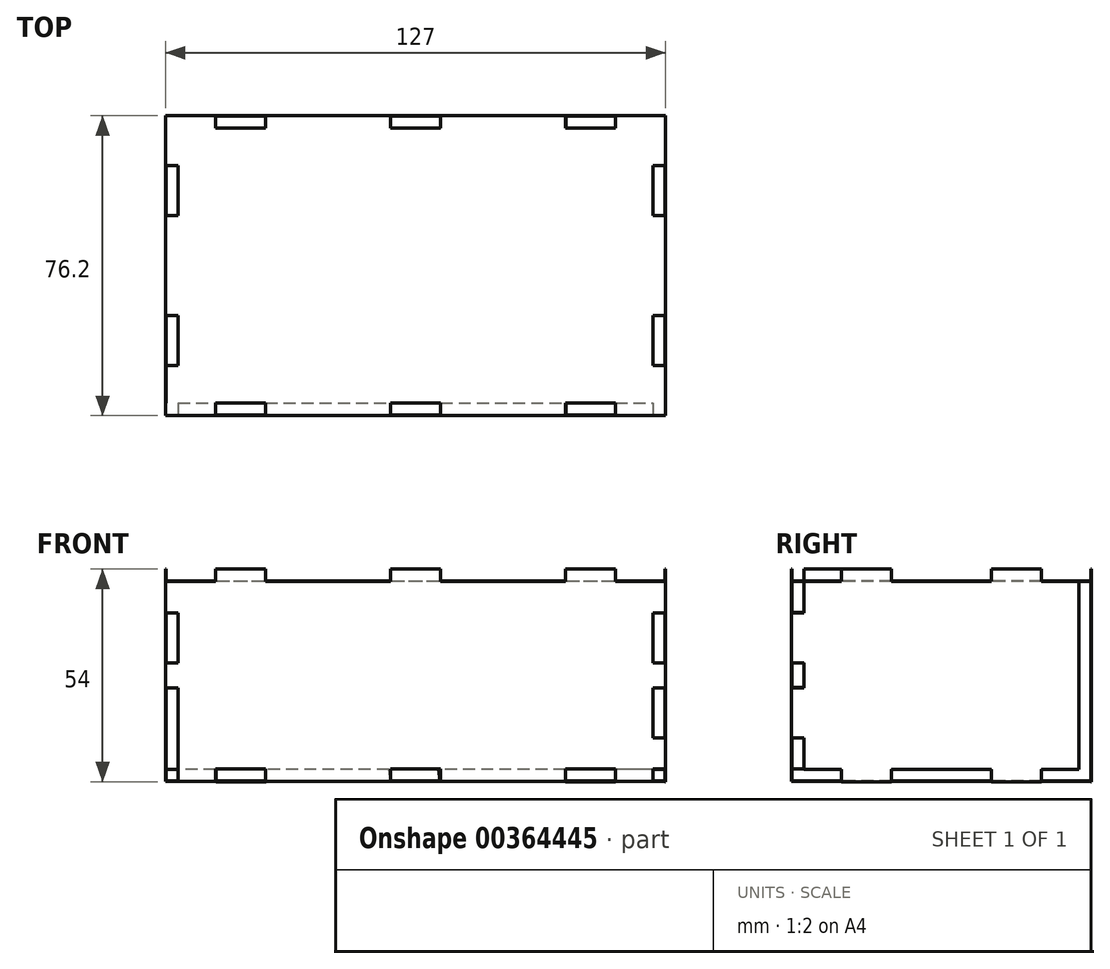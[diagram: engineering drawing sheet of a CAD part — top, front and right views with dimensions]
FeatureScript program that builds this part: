
annotation { "Feature Type Name" : "Feature", "Feature Type Description" : "" }
export const myFeature = defineFeature(function(context is Context, id is Id, definition is map)
    precondition{}
    {
        {
            assignVariable(context, id + "F0", {"name" : "ply", "anyValue" : .125});
        }
        {
            var Q0;
            Q0=qCreatedBy(makeId("Top.planeOp"),FACE);
            var sketch = newSketch(context, id + "F1", { "sketchPlane" : qUnion([Q0])});
            skLineSegment(sketch, "E0.bottom", {"start": v(-63.5, 38.1) * mm, "end": v(63.5, 38.1) * mm});
            skLineSegment(sketch, "E0.top", {"start": v(-63.5, -38.1) * mm, "end": v(63.5, -38.1) * mm});
            skLineSegment(sketch, "E0.left", {"start": v(-63.5, 38.1) * mm, "end": v(-63.5, -38.1) * mm});
            skLineSegment(sketch, "E0.right", {"start": v(63.5, 38.1) * mm, "end": v(63.5, -38.1) * mm});
            skPoint(sketch, "E0.middle", {"position": v(0, 0) * mm});
            skSolve(sketch);
        }
        {
            var Q0;
            Q0=makeQuery(id+"F1.imprint","IMPRINT",FACE,{"disambiguationData":[TD([[makeQuery(id+"F1.imprint","IMPRINT",EDGE,{"derivedFrom":sQuery(id+"F1.wireOp",EDGE,"E0.bottom")}),-1.0]])]});
            extrude(context, id + "F2", {"entities" : qUnion([Q0]), "depth" : (getVariable(context, 'ply')) * mm});
        }
        {
            var Q0;
            Q0=makeQuery(id+"F2.opExtrude","CAP_FACE",FACE,{"disambiguationData":[OSD([sQuery(id+"F1.wireOp",EDGE,"E0.bottom"),sQuery(id+"F1.wireOp",EDGE,"E0.top"),sQuery(id+"F1.wireOp",EDGE,"E0.left"),sQuery(id+"F1.wireOp",EDGE,"E0.right")])],"isStart":false});
            var sketch = newSketch(context, id + "F3", { "sketchPlane" : qUnion([Q0])});
            skLineSegment(sketch, "E1.bottom", {"start": v(-63.5, -25.4) * mm, "end": v(-60.33, -25.4) * mm});
            skLineSegment(sketch, "E1.top", {"start": v(-63.5, -12.7) * mm, "end": v(-60.33, -12.7) * mm});
            skLineSegment(sketch, "E1.left", {"start": v(-63.5, -25.4) * mm, "end": v(-63.5, -12.7) * mm});
            skLineSegment(sketch, "E1.right", {"start": v(-60.33, -25.4) * mm, "end": v(-60.33, -12.7) * mm});
            skLineSegment(sketch, "E2.bottom", {"start": v(-63.5, 12.7) * mm, "end": v(-60.33, 12.7) * mm});
            skLineSegment(sketch, "E2.top", {"start": v(-63.5, 25.4) * mm, "end": v(-60.33, 25.4) * mm});
            skLineSegment(sketch, "E2.left", {"start": v(-63.5, 12.7) * mm, "end": v(-63.5, 25.4) * mm});
            skLineSegment(sketch, "E2.right", {"start": v(-60.33, 12.7) * mm, "end": v(-60.33, 25.4) * mm});
            skSolve(sketch);
        }
        {
            var Q0;
            Q0=makeQuery(id+"F3.imprint","IMPRINT",FACE,{"disambiguationData":[TD([[makeQuery(id+"F3.imprint","IMPRINT",EDGE,{"derivedFrom":sQuery(id+"F3.wireOp",EDGE,"E1.bottom")}),1.0]])]});
            var Q1;
            Q1=makeQuery(id+"F3.imprint","IMPRINT",FACE,{"disambiguationData":[TD([[makeQuery(id+"F3.imprint","IMPRINT",EDGE,{"derivedFrom":sQuery(id+"F3.wireOp",EDGE,"E2.bottom")}),1.0]])]});
            extrude(context, id + "F4", {"entities" : qUnion([Q0, Q1]), "operationType" : NewBodyOperationType.REMOVE, "endBound" : BoundingType.UP_TO_NEXT, "oppositeDirection" : true, "depth" : 25.4 * mm});
        }
        {
            var Q0;
            Q0=makeQuery(id+"F2.opExtrude","CAP_FACE",FACE,{"disambiguationData":[OSD([sQuery(id+"F1.wireOp",EDGE,"E0.bottom"),sQuery(id+"F1.wireOp",EDGE,"E0.top"),sQuery(id+"F1.wireOp",EDGE,"E0.left"),sQuery(id+"F1.wireOp",EDGE,"E0.right")])],"isStart":false});
            var sketch = newSketch(context, id + "F5", { "sketchPlane" : qUnion([Q0])});
            skLineSegment(sketch, "E3.bottom", {"start": v(63.5, 25.4) * mm, "end": v(60.33, 25.4) * mm});
            skLineSegment(sketch, "E3.top", {"start": v(63.5, 12.7) * mm, "end": v(60.33, 12.7) * mm});
            skLineSegment(sketch, "E3.left", {"start": v(63.5, 25.4) * mm, "end": v(63.5, 12.7) * mm});
            skLineSegment(sketch, "E3.right", {"start": v(60.33, 25.4) * mm, "end": v(60.33, 12.7) * mm});
            skLineSegment(sketch, "E4.bottom", {"start": v(63.5, -12.7) * mm, "end": v(60.33, -12.7) * mm});
            skLineSegment(sketch, "E4.top", {"start": v(63.5, -25.4) * mm, "end": v(60.33, -25.4) * mm});
            skLineSegment(sketch, "E4.left", {"start": v(63.5, -12.7) * mm, "end": v(63.5, -25.4) * mm});
            skLineSegment(sketch, "E4.right", {"start": v(60.33, -12.7) * mm, "end": v(60.33, -25.4) * mm});
            skSolve(sketch);
        }
        {
            var Q0;
            Q0=makeQuery(id+"F5.imprint","IMPRINT",FACE,{"disambiguationData":[TD([[makeQuery(id+"F5.imprint","IMPRINT",EDGE,{"derivedFrom":sQuery(id+"F5.wireOp",EDGE,"E3.bottom")}),1.0]])]});
            var Q1;
            Q1=makeQuery(id+"F5.imprint","IMPRINT",FACE,{"disambiguationData":[TD([[makeQuery(id+"F5.imprint","IMPRINT",EDGE,{"derivedFrom":sQuery(id+"F5.wireOp",EDGE,"E4.bottom")}),1.0]])]});
            extrude(context, id + "F6", {"entities" : qUnion([Q0, Q1]), "operationType" : NewBodyOperationType.REMOVE, "endBound" : BoundingType.UP_TO_NEXT, "oppositeDirection" : true, "depth" : 25.4 * mm});
        }
        {
            var Q0;
            Q0=makeQuery(id+"F2.opExtrude","CAP_FACE",FACE,{"disambiguationData":[OSD([sQuery(id+"F1.wireOp",EDGE,"E0.bottom"),sQuery(id+"F1.wireOp",EDGE,"E0.top"),sQuery(id+"F1.wireOp",EDGE,"E0.left"),sQuery(id+"F1.wireOp",EDGE,"E0.right")])],"isStart":false});
            var sketch = newSketch(context, id + "F7", { "sketchPlane" : qUnion([Q0])});
            skLineSegment(sketch, "E5.bottom", {"start": v(-50.8, 38.1) * mm, "end": v(-38.1, 38.1) * mm});
            skLineSegment(sketch, "E5.top", {"start": v(-50.8, 34.93) * mm, "end": v(-38.1, 34.93) * mm});
            skLineSegment(sketch, "E5.left", {"start": v(-50.8, 38.1) * mm, "end": v(-50.8, 34.93) * mm});
            skLineSegment(sketch, "E5.right", {"start": v(-38.1, 38.1) * mm, "end": v(-38.1, 34.93) * mm});
            skLineSegment(sketch, "E6.bottom", {"start": v(-6.35, 38.1) * mm, "end": v(6.35, 38.1) * mm});
            skLineSegment(sketch, "E6.top", {"start": v(-6.35, 34.93) * mm, "end": v(6.35, 34.93) * mm});
            skLineSegment(sketch, "E6.left", {"start": v(-6.35, 38.1) * mm, "end": v(-6.35, 34.93) * mm});
            skLineSegment(sketch, "E6.right", {"start": v(6.35, 38.1) * mm, "end": v(6.35, 34.93) * mm});
            skLineSegment(sketch, "E7.bottom", {"start": v(38.1, 38.1) * mm, "end": v(50.8, 38.1) * mm});
            skLineSegment(sketch, "E7.top", {"start": v(38.1, 34.93) * mm, "end": v(50.8, 34.93) * mm});
            skLineSegment(sketch, "E7.left", {"start": v(38.1, 38.1) * mm, "end": v(38.1, 34.93) * mm});
            skLineSegment(sketch, "E7.right", {"start": v(50.8, 38.1) * mm, "end": v(50.8, 34.93) * mm});
            skSolve(sketch);
        }
        {
            var Q0;
            Q0=makeQuery(id+"F7.imprint","IMPRINT",FACE,{"disambiguationData":[TD([[makeQuery(id+"F7.imprint","IMPRINT",EDGE,{"derivedFrom":sQuery(id+"F7.wireOp",EDGE,"E5.top")}),-1.0]])]});
            var sketch = newSketch(context, id + "F8", { "sketchPlane" : qUnion([Q0])});
            skLineSegment(sketch, "E8.bottom", {"start": v(-50.8, -38.1) * mm, "end": v(-38.1, -38.1) * mm});
            skLineSegment(sketch, "E8.top", {"start": v(-50.8, -34.93) * mm, "end": v(-38.1, -34.93) * mm});
            skLineSegment(sketch, "E8.left", {"start": v(-50.8, -38.1) * mm, "end": v(-50.8, -34.93) * mm});
            skLineSegment(sketch, "E8.right", {"start": v(-38.1, -38.1) * mm, "end": v(-38.1, -34.93) * mm});
            skPoint(sketch, "E9.firstSnap0", {"position": v(-44.45, -38.1) * mm});
            skLineSegment(sketch, "E9.bottom", {"start": v(-6.35, -38.1) * mm, "end": v(6.35, -38.1) * mm});
            skLineSegment(sketch, "E9.top", {"start": v(-6.35, -34.93) * mm, "end": v(6.35, -34.93) * mm});
            skLineSegment(sketch, "E9.left", {"start": v(6.35, -38.1) * mm, "end": v(6.35, -34.93) * mm});
            skLineSegment(sketch, "E9.right", {"start": v(-6.35, -38.1) * mm, "end": v(-6.35, -34.93) * mm});
            skLineSegment(sketch, "E10.bottom", {"start": v(38.1, -38.1) * mm, "end": v(50.8, -38.1) * mm});
            skLineSegment(sketch, "E10.top", {"start": v(38.1, -34.93) * mm, "end": v(50.8, -34.93) * mm});
            skLineSegment(sketch, "E10.left", {"start": v(50.8, -38.1) * mm, "end": v(50.8, -34.93) * mm});
            skLineSegment(sketch, "E10.right", {"start": v(38.1, -38.1) * mm, "end": v(38.1, -34.93) * mm});
            skSolve(sketch);
        }
        {
            var Q0;
            Q0 = qSketchRegion(id + "F7", true);
            extrude(context, id + "F9", {"entities" : qUnion([Q0]), "operationType" : NewBodyOperationType.REMOVE, "endBound" : BoundingType.UP_TO_NEXT, "oppositeDirection" : true, "depth" : 25.4 * mm});
        }
        {
            var Q0;
            Q0 = qSketchRegion(id + "F8", true);
            extrude(context, id + "F10", {"entities" : qUnion([Q0]), "operationType" : NewBodyOperationType.REMOVE, "endBound" : BoundingType.UP_TO_NEXT, "oppositeDirection" : true, "depth" : 25.4 * mm});
        }
        {
            var Q0;
            {var subQ1=sQuery(id+"F1.wireOp",EDGE,"E0.left");var subQ2=sQuery(id+"F1.wireOp",EDGE,"E0.top");Q0=makeQuery(id+"F10.boolean.opBoolean","SPLIT",FACE,{"disambiguationData":[TD([makeQuery(id+"F2.opExtrude","SWEPT_FACE",FACE,{"disambiguationData":[OSD([subQ1])]})])],"derivedFrom":makeQuery(id+"F2.opExtrude","SWEPT_FACE",FACE,{"disambiguationData":[OSD([subQ2])]})});}
            var sketch = newSketch(context, id + "F11", { "sketchPlane" : qUnion([Q0])});
            skLineSegment(sketch, "E11.bottom", {"start": v(-50.8, 3.18) * mm, "end": v(-38.1, 3.18) * mm});
            skLineSegment(sketch, "E11.top", {"start": v(-63.5, -50.8) * mm, "end": v(63.5, -50.8) * mm});
            skLineSegment(sketch, "E11.left", {"start": v(-63.5, 0) * mm, "end": v(-63.5, -50.8) * mm});
            skLineSegment(sketch, "E11.right", {"start": v(63.5, 3.18) * mm, "end": v(63.5, -50.8) * mm});
            skLineSegment(sketch, "E12.top", {"start": v(-63.5, 0) * mm, "end": v(-50.8, 0) * mm});
            skLineSegment(sketch, "E12.right", {"start": v(-50.8, 3.18) * mm, "end": v(-50.8, 0) * mm});
            skLineSegment(sketch, "E13.top", {"start": v(-38.1, 0) * mm, "end": v(-6.35, 0) * mm});
            skLineSegment(sketch, "E13.left", {"start": v(-38.1, 3.18) * mm, "end": v(-38.1, 0) * mm});
            skLineSegment(sketch, "E13.right", {"start": v(-6.35, 3.18) * mm, "end": v(-6.35, 0) * mm});
            skLineSegment(sketch, "E14.top", {"start": v(6.35, 0) * mm, "end": v(38.1, 0) * mm});
            skLineSegment(sketch, "E14.left", {"start": v(6.35, 3.18) * mm, "end": v(6.35, 0) * mm});
            skLineSegment(sketch, "E14.right", {"start": v(38.1, 3.18) * mm, "end": v(38.1, 0) * mm});
            skLineSegment(sketch, "E15.top", {"start": v(50.8, 0) * mm, "end": v(63.5, 0) * mm});
            skLineSegment(sketch, "E15.left", {"start": v(50.8, 3.18) * mm, "end": v(50.8, 0) * mm});
            skLineSegment(sketch, "E15.right", {"start": v(63.5, 3.18) * mm, "end": v(63.5, 0) * mm});
            skPoint(sketch, "E12.left.start.orphan", {"position": v(-63.5, 3.18) * mm});
            skLineSegment(sketch, "E16.trimOffspring", {"start": v(-6.35, 3.18) * mm, "end": v(6.35, 3.18) * mm});
            skLineSegment(sketch, "E17.trimOffspring", {"start": v(38.1, 3.18) * mm, "end": v(50.8, 3.18) * mm});
            skSolve(sketch);
        }
        {
            var Q0;
            Q0=makeQuery(id+"F11.imprint","IMPRINT",FACE,{"disambiguationData":[TD([[makeQuery(id+"F11.imprint","IMPRINT",EDGE,{"derivedFrom":sQuery(id+"F11.wireOp",EDGE,"E11.bottom")}),-1.0]])]});
            extrude(context, id + "F12", {"entities" : qUnion([Q0]), "oppositeDirection" : true, "depth" : (getVariable(context, 'ply')) * mm});
        }
        {
            var Q0;
            Q0=makeQuery(id+"F12.opExtrude","CAP_FACE",FACE,{"disambiguationData":[OSD([sQuery(id+"F11.wireOp",EDGE,"E11.bottom"),sQuery(id+"F11.wireOp",EDGE,"E11.top"),sQuery(id+"F11.wireOp",EDGE,"E11.left"),sQuery(id+"F11.wireOp",EDGE,"E11.right"),sQuery(id+"F11.wireOp",EDGE,"E12.top"),sQuery(id+"F11.wireOp",EDGE,"E12.right"),sQuery(id+"F11.wireOp",EDGE,"E13.top"),sQuery(id+"F11.wireOp",EDGE,"E13.left"),sQuery(id+"F11.wireOp",EDGE,"E13.right"),sQuery(id+"F11.wireOp",EDGE,"E14.top"),sQuery(id+"F11.wireOp",EDGE,"E14.left"),sQuery(id+"F11.wireOp",EDGE,"E14.right"),sQuery(id+"F11.wireOp",EDGE,"E15.top"),sQuery(id+"F11.wireOp",EDGE,"E15.left"),sQuery(id+"F11.wireOp",EDGE,"E16.trimOffspring"),sQuery(id+"F11.wireOp",EDGE,"E17.trimOffspring")])],"isStart":true});
            var sketch = newSketch(context, id + "F13", { "sketchPlane" : qUnion([Q0])});
            skLineSegment(sketch, "E18.bottom", {"start": v(-50.8, -50.8) * mm, "end": v(-38.1, -50.8) * mm});
            skLineSegment(sketch, "E18.top", {"start": v(-50.8, -47.63) * mm, "end": v(-38.1, -47.63) * mm});
            skLineSegment(sketch, "E18.left", {"start": v(-50.8, -50.8) * mm, "end": v(-50.8, -47.63) * mm});
            skLineSegment(sketch, "E18.right", {"start": v(-38.1, -50.8) * mm, "end": v(-38.1, -47.63) * mm});
            skLineSegment(sketch, "E19.bottom", {"start": v(-6.35, -50.8) * mm, "end": v(6.35, -50.8) * mm});
            skLineSegment(sketch, "E19.top", {"start": v(-6.35, -47.62) * mm, "end": v(6.35, -47.62) * mm});
            skLineSegment(sketch, "E19.left", {"start": v(-6.35, -50.8) * mm, "end": v(-6.35, -47.62) * mm});
            skLineSegment(sketch, "E19.right", {"start": v(6.35, -50.8) * mm, "end": v(6.35, -47.62) * mm});
            skLineSegment(sketch, "E20.bottom", {"start": v(38.1, -50.8) * mm, "end": v(50.8, -50.8) * mm});
            skLineSegment(sketch, "E20.top", {"start": v(38.1, -47.62) * mm, "end": v(50.8, -47.62) * mm});
            skLineSegment(sketch, "E20.left", {"start": v(38.1, -50.8) * mm, "end": v(38.1, -47.62) * mm});
            skLineSegment(sketch, "E20.right", {"start": v(50.8, -50.8) * mm, "end": v(50.8, -47.62) * mm});
            skSolve(sketch);
        }
        {
            var Q0;
            Q0 = qSketchRegion(id + "F13", true);
            extrude(context, id + "F14", {"entities" : qUnion([Q0]), "operationType" : NewBodyOperationType.REMOVE, "endBound" : BoundingType.UP_TO_NEXT, "oppositeDirection" : true, "depth" : 25.4 * mm});
        }
        {
            var Q0;
            Q0=makeQuery(id+"F12.opExtrude","CAP_FACE",FACE,{"disambiguationData":[OSD([sQuery(id+"F11.wireOp",EDGE,"E11.bottom"),sQuery(id+"F11.wireOp",EDGE,"E11.top"),sQuery(id+"F11.wireOp",EDGE,"E11.left"),sQuery(id+"F11.wireOp",EDGE,"E11.right"),sQuery(id+"F11.wireOp",EDGE,"E12.top"),sQuery(id+"F11.wireOp",EDGE,"E12.right"),sQuery(id+"F11.wireOp",EDGE,"E13.top"),sQuery(id+"F11.wireOp",EDGE,"E13.left"),sQuery(id+"F11.wireOp",EDGE,"E13.right"),sQuery(id+"F11.wireOp",EDGE,"E14.top"),sQuery(id+"F11.wireOp",EDGE,"E14.left"),sQuery(id+"F11.wireOp",EDGE,"E14.right"),sQuery(id+"F11.wireOp",EDGE,"E15.top"),sQuery(id+"F11.wireOp",EDGE,"E15.left"),sQuery(id+"F11.wireOp",EDGE,"E16.trimOffspring"),sQuery(id+"F11.wireOp",EDGE,"E17.trimOffspring")])],"isStart":true});
            var sketch = newSketch(context, id + "F15", { "sketchPlane" : qUnion([Q0])});
            skPoint(sketch, "E21.oppositeSnap0", {"position": v(-63.5, -25.4) * mm});
            skPoint(sketch, "E21.oppositeSnap1", {"position": v(-57.15, 0) * mm});
            skLineSegment(sketch, "E21.bottom", {"start": v(-63.5, -7.94) * mm, "end": v(-60.33, -7.94) * mm});
            skLineSegment(sketch, "E21.top", {"start": v(-63.5, -20.64) * mm, "end": v(-60.33, -20.64) * mm});
            skLineSegment(sketch, "E21.left", {"start": v(-63.5, -7.94) * mm, "end": v(-63.5, -20.64) * mm});
            skLineSegment(sketch, "E21.right", {"start": v(-60.33, -7.94) * mm, "end": v(-60.33, -20.64) * mm});
            skLineSegment(sketch, "E22.bottom", {"start": v(-63.5, -26.99) * mm, "end": v(-60.33, -26.99) * mm});
            skLineSegment(sketch, "E22.top", {"start": v(-63.5, -39.69) * mm, "end": v(-60.33, -39.69) * mm});
            skLineSegment(sketch, "E22.left", {"start": v(-63.5, -26.99) * mm, "end": v(-63.5, -39.69) * mm});
            skLineSegment(sketch, "E22.right", {"start": v(-60.33, -26.99) * mm, "end": v(-60.33, -39.69) * mm});
            skSolve(sketch);
        }
        {
            var Q0;
            Q0 = qSketchRegion(id + "F15", true);
            extrude(context, id + "F16", {"entities" : qUnion([Q0]), "operationType" : NewBodyOperationType.REMOVE, "endBound" : BoundingType.UP_TO_NEXT, "oppositeDirection" : true, "depth" : 25.4 * mm});
        }
        {
            var Q0;
            Q0=makeQuery(id+"F12.opExtrude","CAP_FACE",FACE,{"disambiguationData":[OSD([sQuery(id+"F11.wireOp",EDGE,"E11.bottom"),sQuery(id+"F11.wireOp",EDGE,"E11.top"),sQuery(id+"F11.wireOp",EDGE,"E11.left"),sQuery(id+"F11.wireOp",EDGE,"E11.right"),sQuery(id+"F11.wireOp",EDGE,"E12.top"),sQuery(id+"F11.wireOp",EDGE,"E12.right"),sQuery(id+"F11.wireOp",EDGE,"E13.top"),sQuery(id+"F11.wireOp",EDGE,"E13.left"),sQuery(id+"F11.wireOp",EDGE,"E13.right"),sQuery(id+"F11.wireOp",EDGE,"E14.top"),sQuery(id+"F11.wireOp",EDGE,"E14.left"),sQuery(id+"F11.wireOp",EDGE,"E14.right"),sQuery(id+"F11.wireOp",EDGE,"E15.top"),sQuery(id+"F11.wireOp",EDGE,"E15.left"),sQuery(id+"F11.wireOp",EDGE,"E16.trimOffspring"),sQuery(id+"F11.wireOp",EDGE,"E17.trimOffspring")])],"isStart":true});
            var sketch = newSketch(context, id + "F17", { "sketchPlane" : qUnion([Q0])});
            skLineSegment(sketch, "E23.bottom", {"start": v(63.5, -7.94) * mm, "end": v(60.32, -7.94) * mm});
            skLineSegment(sketch, "E23.top", {"start": v(63.5, -20.64) * mm, "end": v(60.32, -20.64) * mm});
            skLineSegment(sketch, "E23.left", {"start": v(63.5, -7.94) * mm, "end": v(63.5, -20.64) * mm});
            skLineSegment(sketch, "E23.right", {"start": v(60.32, -7.94) * mm, "end": v(60.32, -20.64) * mm});
            skLineSegment(sketch, "E24.bottom", {"start": v(63.5, -26.99) * mm, "end": v(60.32, -26.99) * mm});
            skLineSegment(sketch, "E24.top", {"start": v(63.5, -39.69) * mm, "end": v(60.32, -39.69) * mm});
            skLineSegment(sketch, "E24.left", {"start": v(63.5, -26.99) * mm, "end": v(63.5, -39.69) * mm});
            skLineSegment(sketch, "E24.right", {"start": v(60.32, -26.99) * mm, "end": v(60.32, -39.69) * mm});
            skLineSegment(sketch, "E25.bottom", {"start": v(-63.5, -39.69) * mm, "end": v(-60.33, -39.69) * mm});
            skLineSegment(sketch, "E25.top", {"start": v(-63.5, -50.8) * mm, "end": v(-60.33, -50.8) * mm});
            skLineSegment(sketch, "E25.left", {"start": v(-63.5, -39.69) * mm, "end": v(-63.5, -50.8) * mm});
            skLineSegment(sketch, "E25.right", {"start": v(-60.33, -39.69) * mm, "end": v(-60.33, -50.8) * mm});
            skSolve(sketch);
        }
        {
            var Q0;
            Q0 = qSketchRegion(id + "F17", true);
            extrude(context, id + "F18", {"entities" : qUnion([Q0]), "operationType" : NewBodyOperationType.REMOVE, "endBound" : BoundingType.UP_TO_NEXT, "oppositeDirection" : true, "depth" : 25.4 * mm});
        }
        {
            var Q0;
            {var subQ13=sQuery(id+"F11.wireOp",EDGE,"E11.left");var subQ14=sQuery(id+"F11.wireOp",EDGE,"E11.top");Q0=makeQuery(id+"F14.boolean.opBoolean","SPLIT",FACE,{"disambiguationData":[TD([makeQuery(id+"F12.opExtrude","SWEPT_FACE",FACE,{"disambiguationData":[OSD([subQ13])]})])],"derivedFrom":makeQuery(id+"F12.opExtrude","SWEPT_FACE",FACE,{"disambiguationData":[OSD([subQ14])]})});}
            var sketch = newSketch(context, id + "F19", { "sketchPlane" : qUnion([Q0])});
            skLineSegment(sketch, "E26.bottom", {"start": v(-50.8, 38.1) * mm, "end": v(-38.15, 38.1) * mm});
            skLineSegment(sketch, "E26.top", {"start": v(-63.5, -38.1) * mm, "end": v(63.5, -38.1) * mm});
            skLineSegment(sketch, "E26.left", {"start": v(-63.5, 34.92) * mm, "end": v(-63.5, -38.1) * mm});
            skLineSegment(sketch, "E26.right", {"start": v(63.5, 38.1) * mm, "end": v(63.5, -38.1) * mm});
            skLineSegment(sketch, "E27.top", {"start": v(-63.5, 34.92) * mm, "end": v(-50.8, 34.92) * mm});
            skLineSegment(sketch, "E27.right", {"start": v(-50.8, 38.1) * mm, "end": v(-50.8, 34.92) * mm});
            skLineSegment(sketch, "E28.top", {"start": v(-38.15, 34.92) * mm, "end": v(-6.4, 34.92) * mm});
            skLineSegment(sketch, "E28.left", {"start": v(-38.15, 38.1) * mm, "end": v(-38.15, 34.92) * mm});
            skLineSegment(sketch, "E28.right", {"start": v(-6.4, 38.1) * mm, "end": v(-6.4, 34.92) * mm});
            skLineSegment(sketch, "E29.top", {"start": v(6.42, 34.92) * mm, "end": v(38.17, 34.92) * mm});
            skLineSegment(sketch, "E29.left", {"start": v(6.42, 38.1) * mm, "end": v(6.42, 34.92) * mm});
            skLineSegment(sketch, "E29.right", {"start": v(38.17, 38.1) * mm, "end": v(38.17, 34.92) * mm});
            skLineSegment(sketch, "E30.top", {"start": v(50.8, 34.92) * mm, "end": v(63.5, 34.92) * mm});
            skLineSegment(sketch, "E30.left", {"start": v(50.8, 38.1) * mm, "end": v(50.8, 34.92) * mm});
            skLineSegment(sketch, "E30.right", {"start": v(63.5, 38.1) * mm, "end": v(63.5, 34.92) * mm});
            skLineSegment(sketch, "E31.trimOffspring", {"start": v(-6.4, 38.1) * mm, "end": v(6.42, 38.1) * mm});
            skLineSegment(sketch, "E32.trimOffspring", {"start": v(38.17, 38.1) * mm, "end": v(50.8, 38.1) * mm});
            skLineSegment(sketch, "E33.bottom", {"start": v(-63.5, 34.92) * mm, "end": v(-60.33, 34.92) * mm});
            skLineSegment(sketch, "E33.top", {"start": v(-63.5, 38.1) * mm, "end": v(-60.33, 38.1) * mm});
            skLineSegment(sketch, "E33.left", {"start": v(-63.5, 34.92) * mm, "end": v(-63.5, 38.1) * mm});
            skLineSegment(sketch, "E33.right", {"start": v(-60.33, 34.92) * mm, "end": v(-60.33, 38.1) * mm});
            skLineSegment(sketch, "E34.bottom", {"start": v(63.5, 34.92) * mm, "end": v(60.34, 34.92) * mm});
            skLineSegment(sketch, "E34.top", {"start": v(63.5, 38.1) * mm, "end": v(60.34, 38.1) * mm});
            skLineSegment(sketch, "E34.left", {"start": v(63.5, 34.92) * mm, "end": v(63.5, 38.1) * mm});
            skLineSegment(sketch, "E34.right", {"start": v(60.34, 34.92) * mm, "end": v(60.34, 38.1) * mm});
            skSolve(sketch);
        }
        {
            var Q0;
            Q0 = qSketchRegion(id + "F19", true);
            extrude(context, id + "F20", {"entities" : qUnion([Q0]), "oppositeDirection" : true, "depth" : (getVariable(context, 'ply')) * mm});
        }
        {
            var Q0;
            Q0=makeQuery(id+"F20.opExtrude","CAP_FACE",FACE,{"disambiguationData":[OSD([sQuery(id+"F19.wireOp",EDGE,"E26.bottom"),sQuery(id+"F19.wireOp",EDGE,"E26.top"),sQuery(id+"F19.wireOp",EDGE,"E26.left"),sQuery(id+"F19.wireOp",EDGE,"E26.right"),sQuery(id+"F19.wireOp",EDGE,"E27.top"),sQuery(id+"F19.wireOp",EDGE,"E27.right"),sQuery(id+"F19.wireOp",EDGE,"E28.top"),sQuery(id+"F19.wireOp",EDGE,"E28.left"),sQuery(id+"F19.wireOp",EDGE,"E28.right"),sQuery(id+"F19.wireOp",EDGE,"E29.top"),sQuery(id+"F19.wireOp",EDGE,"E29.left"),sQuery(id+"F19.wireOp",EDGE,"E29.right"),sQuery(id+"F19.wireOp",EDGE,"E30.top"),sQuery(id+"F19.wireOp",EDGE,"E30.left"),sQuery(id+"F19.wireOp",EDGE,"E31.trimOffspring"),sQuery(id+"F19.wireOp",EDGE,"E32.trimOffspring")])],"isStart":true});
            var sketch = newSketch(context, id + "F21", { "sketchPlane" : qUnion([Q0])});
            skLineSegment(sketch, "E35.bottom", {"start": v(-50.8, -38.1) * mm, "end": v(-38.15, -38.1) * mm});
            skLineSegment(sketch, "E35.top", {"start": v(-50.8, -34.93) * mm, "end": v(-38.15, -34.93) * mm});
            skLineSegment(sketch, "E35.left", {"start": v(-50.8, -38.1) * mm, "end": v(-50.8, -34.93) * mm});
            skLineSegment(sketch, "E35.right", {"start": v(-38.15, -38.1) * mm, "end": v(-38.15, -34.93) * mm});
            skLineSegment(sketch, "E36.bottom", {"start": v(-6.4, -38.1) * mm, "end": v(6.42, -38.1) * mm});
            skLineSegment(sketch, "E36.top", {"start": v(-6.4, -34.93) * mm, "end": v(6.42, -34.93) * mm});
            skLineSegment(sketch, "E36.left", {"start": v(-6.4, -38.1) * mm, "end": v(-6.4, -34.93) * mm});
            skLineSegment(sketch, "E36.right", {"start": v(6.42, -38.1) * mm, "end": v(6.42, -34.93) * mm});
            skLineSegment(sketch, "E37.bottom", {"start": v(38.17, -38.1) * mm, "end": v(50.8, -38.1) * mm});
            skLineSegment(sketch, "E37.top", {"start": v(38.17, -34.93) * mm, "end": v(50.8, -34.93) * mm});
            skLineSegment(sketch, "E37.left", {"start": v(38.17, -38.1) * mm, "end": v(38.17, -34.93) * mm});
            skLineSegment(sketch, "E37.right", {"start": v(50.8, -38.1) * mm, "end": v(50.8, -34.93) * mm});
            skSolve(sketch);
        }
        {
            var Q0;
            Q0 = qSketchRegion(id + "F21", true);
            extrude(context, id + "F22", {"entities" : qUnion([Q0]), "operationType" : NewBodyOperationType.REMOVE, "endBound" : BoundingType.UP_TO_NEXT, "oppositeDirection" : true, "depth" : 25.4 * mm});
        }
        {
            var Q0;
            Q0=makeQuery(id+"F20.opExtrude","CAP_FACE",FACE,{"disambiguationData":[OSD([sQuery(id+"F19.wireOp",EDGE,"E26.bottom"),sQuery(id+"F19.wireOp",EDGE,"E26.top"),sQuery(id+"F19.wireOp",EDGE,"E26.left"),sQuery(id+"F19.wireOp",EDGE,"E26.right"),sQuery(id+"F19.wireOp",EDGE,"E27.top"),sQuery(id+"F19.wireOp",EDGE,"E27.right"),sQuery(id+"F19.wireOp",EDGE,"E28.top"),sQuery(id+"F19.wireOp",EDGE,"E28.left"),sQuery(id+"F19.wireOp",EDGE,"E28.right"),sQuery(id+"F19.wireOp",EDGE,"E29.top"),sQuery(id+"F19.wireOp",EDGE,"E29.left"),sQuery(id+"F19.wireOp",EDGE,"E29.right"),sQuery(id+"F19.wireOp",EDGE,"E30.top"),sQuery(id+"F19.wireOp",EDGE,"E30.left"),sQuery(id+"F19.wireOp",EDGE,"E31.trimOffspring"),sQuery(id+"F19.wireOp",EDGE,"E32.trimOffspring")])],"isStart":true});
            var sketch = newSketch(context, id + "F23", { "sketchPlane" : qUnion([Q0])});
            skLineSegment(sketch, "E38.bottom", {"start": v(-63.5, 25.4) * mm, "end": v(-60.33, 25.4) * mm});
            skLineSegment(sketch, "E38.top", {"start": v(-63.5, 12.7) * mm, "end": v(-60.33, 12.7) * mm});
            skLineSegment(sketch, "E38.left", {"start": v(-63.5, 25.4) * mm, "end": v(-63.5, 12.7) * mm});
            skLineSegment(sketch, "E38.right", {"start": v(-60.33, 25.4) * mm, "end": v(-60.33, 12.7) * mm});
            skLineSegment(sketch, "E39.bottom", {"start": v(-63.5, -12.7) * mm, "end": v(-60.33, -12.7) * mm});
            skLineSegment(sketch, "E39.top", {"start": v(-63.5, -25.4) * mm, "end": v(-60.33, -25.4) * mm});
            skLineSegment(sketch, "E39.left", {"start": v(-63.5, -12.7) * mm, "end": v(-63.5, -25.4) * mm});
            skLineSegment(sketch, "E39.right", {"start": v(-60.33, -12.7) * mm, "end": v(-60.33, -25.4) * mm});
            skSolve(sketch);
        }
        {
            var Q0;
            Q0 = qSketchRegion(id + "F23", true);
            extrude(context, id + "F24", {"entities" : qUnion([Q0]), "operationType" : NewBodyOperationType.REMOVE, "endBound" : BoundingType.UP_TO_NEXT, "oppositeDirection" : true, "depth" : 25.4 * mm});
        }
        {
            var Q0;
            Q0=makeQuery(id+"F20.opExtrude","CAP_FACE",FACE,{"disambiguationData":[OSD([sQuery(id+"F19.wireOp",EDGE,"E26.bottom"),sQuery(id+"F19.wireOp",EDGE,"E26.top"),sQuery(id+"F19.wireOp",EDGE,"E26.left"),sQuery(id+"F19.wireOp",EDGE,"E26.right"),sQuery(id+"F19.wireOp",EDGE,"E27.top"),sQuery(id+"F19.wireOp",EDGE,"E27.right"),sQuery(id+"F19.wireOp",EDGE,"E28.top"),sQuery(id+"F19.wireOp",EDGE,"E28.left"),sQuery(id+"F19.wireOp",EDGE,"E28.right"),sQuery(id+"F19.wireOp",EDGE,"E29.top"),sQuery(id+"F19.wireOp",EDGE,"E29.left"),sQuery(id+"F19.wireOp",EDGE,"E29.right"),sQuery(id+"F19.wireOp",EDGE,"E30.top"),sQuery(id+"F19.wireOp",EDGE,"E30.left"),sQuery(id+"F19.wireOp",EDGE,"E31.trimOffspring"),sQuery(id+"F19.wireOp",EDGE,"E32.trimOffspring")])],"isStart":true});
            var sketch = newSketch(context, id + "F25", { "sketchPlane" : qUnion([Q0])});
            skLineSegment(sketch, "E40.bottom", {"start": v(63.5, 25.4) * mm, "end": v(60.33, 25.4) * mm});
            skLineSegment(sketch, "E40.top", {"start": v(63.5, 12.7) * mm, "end": v(60.33, 12.7) * mm});
            skLineSegment(sketch, "E40.left", {"start": v(63.5, 25.4) * mm, "end": v(63.5, 12.7) * mm});
            skLineSegment(sketch, "E40.right", {"start": v(60.33, 25.4) * mm, "end": v(60.33, 12.7) * mm});
            skLineSegment(sketch, "E41.bottom", {"start": v(63.5, -12.7) * mm, "end": v(60.33, -12.7) * mm});
            skLineSegment(sketch, "E41.top", {"start": v(63.5, -25.4) * mm, "end": v(60.33, -25.4) * mm});
            skLineSegment(sketch, "E41.left", {"start": v(63.5, -12.7) * mm, "end": v(63.5, -25.4) * mm});
            skLineSegment(sketch, "E41.right", {"start": v(60.33, -12.7) * mm, "end": v(60.33, -25.4) * mm});
            skSolve(sketch);
        }
        {
            var Q0;
            Q0 = qSketchRegion(id + "F25", true);
            extrude(context, id + "F26", {"entities" : qUnion([Q0]), "operationType" : NewBodyOperationType.REMOVE, "endBound" : BoundingType.UP_TO_NEXT, "oppositeDirection" : true, "depth" : 25.4 * mm});
        }
        {
            var Q0;
            {var subQ0=sQuery(id+"F1.wireOp",EDGE,"E0.bottom");var subQ2=sQuery(id+"F1.wireOp",EDGE,"E0.left");Q0=makeQuery(id+"F4.boolean.opBoolean","SPLIT",FACE,{"disambiguationData":[TD([makeQuery(id+"F2.opExtrude","SWEPT_FACE",FACE,{"disambiguationData":[OSD([subQ0])]})])],"derivedFrom":makeQuery(id+"F2.opExtrude","SWEPT_FACE",FACE,{"disambiguationData":[OSD([subQ2])]})});}
            var sketch = newSketch(context, id + "F27", { "sketchPlane" : qUnion([Q0])});
            skLineSegment(sketch, "E42.bottom", {"start": v(-25.4, 3.18) * mm, "end": v(-12.7, 3.18) * mm});
            skLineSegment(sketch, "E42.top", {"start": v(-25.4, -50.8) * mm, "end": v(-12.7, -50.8) * mm});
            skLineSegment(sketch, "E42.left", {"start": v(-34.92, 0) * mm, "end": v(-34.92, -47.63) * mm});
            skLineSegment(sketch, "E42.right", {"start": v(34.93, 3.18) * mm, "end": v(34.93, -47.62) * mm});
            skLineSegment(sketch, "E43.top", {"start": v(-34.92, 0) * mm, "end": v(-25.4, 0) * mm});
            skLineSegment(sketch, "E43.right", {"start": v(-25.4, 3.18) * mm, "end": v(-25.4, 0) * mm});
            skLineSegment(sketch, "E44.top", {"start": v(-12.7, 0) * mm, "end": v(12.7, 0) * mm});
            skLineSegment(sketch, "E44.left", {"start": v(-12.7, 3.17) * mm, "end": v(-12.7, 0) * mm});
            skLineSegment(sketch, "E44.right", {"start": v(12.7, 3.18) * mm, "end": v(12.7, 0) * mm});
            skLineSegment(sketch, "E45.top", {"start": v(34.93, 3.18) * mm, "end": v(22.23, 3.18) * mm});
            skLineSegment(sketch, "E45.right", {"start": v(25.4, 3.18) * mm, "end": v(22.23, 3.18) * mm});
            skLineSegment(sketch, "E46.top", {"start": v(-34.92, -47.63) * mm, "end": v(-25.4, -47.63) * mm});
            skLineSegment(sketch, "E46.right", {"start": v(-25.4, -50.8) * mm, "end": v(-25.4, -47.63) * mm});
            skLineSegment(sketch, "E47.top", {"start": v(-12.7, -47.62) * mm, "end": v(12.7, -47.62) * mm});
            skLineSegment(sketch, "E47.left", {"start": v(-12.7, -50.8) * mm, "end": v(-12.7, -47.62) * mm});
            skLineSegment(sketch, "E47.right", {"start": v(12.7, -50.8) * mm, "end": v(12.7, -47.62) * mm});
            skLineSegment(sketch, "E48.top", {"start": v(25.4, -47.63) * mm, "end": v(34.93, -47.63) * mm});
            skLineSegment(sketch, "E48.left", {"start": v(25.4, -50.8) * mm, "end": v(25.4, -47.62) * mm});
            skLineSegment(sketch, "E49.trimOffspring", {"start": v(12.7, 3.18) * mm, "end": v(25.4, 3.18) * mm});
            skLineSegment(sketch, "E50.trimOffspring", {"start": v(12.7, -50.8) * mm, "end": v(25.4, -50.8) * mm});
            skLineSegment(sketch, "E51.bottom", {"start": v(34.93, -7.8) * mm, "end": v(38, -7.8) * mm});
            skLineSegment(sketch, "E51.top", {"start": v(34.93, -20.5) * mm, "end": v(38, -20.5) * mm});
            skLineSegment(sketch, "E51.left", {"start": v(34.93, -7.8) * mm, "end": v(34.93, -20.5) * mm});
            skLineSegment(sketch, "E51.right", {"start": v(38, -7.8) * mm, "end": v(38, -20.5) * mm});
            skPoint(sketch, "E52.oppositeSnap0", {"position": v(38, -14.15) * mm});
            skLineSegment(sketch, "E52.bottom", {"start": v(34.93, -26.89) * mm, "end": v(38, -26.89) * mm});
            skLineSegment(sketch, "E52.top", {"start": v(34.93, -47.63) * mm, "end": v(38, -47.63) * mm});
            skLineSegment(sketch, "E52.left", {"start": v(34.93, -26.89) * mm, "end": v(34.93, -47.63) * mm});
            skLineSegment(sketch, "E52.right", {"start": v(38, -26.89) * mm, "end": v(38, -47.63) * mm});
            skSolve(sketch);
        }
        {
            var Q0;
            Q0 = qSketchRegion(id + "F27", true);
            extrude(context, id + "F28", {"entities" : qUnion([Q0]), "oppositeDirection" : true, "depth" : (getVariable(context, 'ply')) * mm});
        }
        {
            var Q0;
            Q0=makeQuery(id+"F12.opExtrude","CAP_FACE",FACE,{"disambiguationData":[OSD([sQuery(id+"F11.wireOp",EDGE,"E11.bottom"),sQuery(id+"F11.wireOp",EDGE,"E11.top"),sQuery(id+"F11.wireOp",EDGE,"E11.left"),sQuery(id+"F11.wireOp",EDGE,"E11.right"),sQuery(id+"F11.wireOp",EDGE,"E12.top"),sQuery(id+"F11.wireOp",EDGE,"E12.right"),sQuery(id+"F11.wireOp",EDGE,"E13.top"),sQuery(id+"F11.wireOp",EDGE,"E13.left"),sQuery(id+"F11.wireOp",EDGE,"E13.right"),sQuery(id+"F11.wireOp",EDGE,"E14.top"),sQuery(id+"F11.wireOp",EDGE,"E14.left"),sQuery(id+"F11.wireOp",EDGE,"E14.right"),sQuery(id+"F11.wireOp",EDGE,"E15.top"),sQuery(id+"F11.wireOp",EDGE,"E15.left"),sQuery(id+"F11.wireOp",EDGE,"E16.trimOffspring"),sQuery(id+"F11.wireOp",EDGE,"E17.trimOffspring")])],"isStart":true});
            var sketch = newSketch(context, id + "F29", { "sketchPlane" : qUnion([Q0])});
            skLineSegment(sketch, "E53.bottom", {"start": v(63.5, -50.8) * mm, "end": v(60.32, -50.8) * mm});
            skLineSegment(sketch, "E53.top", {"start": v(63.5, -47.62) * mm, "end": v(60.32, -47.62) * mm});
            skLineSegment(sketch, "E53.left", {"start": v(63.5, -50.8) * mm, "end": v(63.5, -47.62) * mm});
            skLineSegment(sketch, "E53.right", {"start": v(60.32, -50.8) * mm, "end": v(60.32, -47.62) * mm});
            skSolve(sketch);
        }
        {
            var Q0;
            Q0 = qSketchRegion(id + "F29", true);
            extrude(context, id + "F30", {"entities" : qUnion([Q0]), "operationType" : NewBodyOperationType.REMOVE, "endBound" : BoundingType.UP_TO_NEXT, "oppositeDirection" : true, "depth" : 25.4 * mm});
        }
        {
            var Q0;
            {var subQ0=sQuery(id+"F1.wireOp",EDGE,"E0.right");var subQ2=sQuery(id+"F1.wireOp",EDGE,"E0.top");Q0=makeQuery(id+"F6.boolean.opBoolean","SPLIT",FACE,{"disambiguationData":[TD([makeQuery(id+"F2.opExtrude","SWEPT_FACE",FACE,{"disambiguationData":[OSD([subQ2])]})])],"derivedFrom":makeQuery(id+"F2.opExtrude","SWEPT_FACE",FACE,{"disambiguationData":[OSD([subQ0])]})});}
            var sketch = newSketch(context, id + "F31", { "sketchPlane" : qUnion([Q0])});
            skLineSegment(sketch, "E54.bottom", {"start": v(-34.92, 0) * mm, "end": v(-25.4, 0) * mm});
            skLineSegment(sketch, "E54.top", {"start": v(-34.92, -47.65) * mm, "end": v(-25.4, -47.65) * mm});
            skLineSegment(sketch, "E54.left", {"start": v(-34.92, 0) * mm, "end": v(-34.92, -7.94) * mm});
            skLineSegment(sketch, "E54.right", {"start": v(34.93, 0) * mm, "end": v(34.93, -47.65) * mm});
            skLineSegment(sketch, "E55.top", {"start": v(-25.4, 3.17) * mm, "end": v(-12.7, 3.17) * mm});
            skLineSegment(sketch, "E55.left", {"start": v(-25.4, 0) * mm, "end": v(-25.4, 3.17) * mm});
            skLineSegment(sketch, "E55.right", {"start": v(-12.7, 0) * mm, "end": v(-12.7, 3.17) * mm});
            skLineSegment(sketch, "E56.top", {"start": v(12.7, 3.18) * mm, "end": v(25.4, 3.18) * mm});
            skLineSegment(sketch, "E56.left", {"start": v(12.7, 0) * mm, "end": v(12.7, 3.18) * mm});
            skLineSegment(sketch, "E56.right", {"start": v(25.4, 0) * mm, "end": v(25.4, 3.18) * mm});
            skLineSegment(sketch, "E57.top", {"start": v(-25.4, -50.83) * mm, "end": v(-12.7, -50.83) * mm});
            skLineSegment(sketch, "E57.left", {"start": v(-25.4, -47.65) * mm, "end": v(-25.4, -50.83) * mm});
            skLineSegment(sketch, "E57.right", {"start": v(-12.7, -47.65) * mm, "end": v(-12.7, -50.83) * mm});
            skLineSegment(sketch, "E58.top", {"start": v(12.7, -50.83) * mm, "end": v(25.4, -50.83) * mm});
            skLineSegment(sketch, "E58.left", {"start": v(12.7, -47.65) * mm, "end": v(12.7, -50.83) * mm});
            skLineSegment(sketch, "E58.right", {"start": v(25.4, -47.65) * mm, "end": v(25.4, -50.83) * mm});
            skLineSegment(sketch, "E59.bottom", {"start": v(-34.92, -7.94) * mm, "end": v(-38.1, -7.94) * mm});
            skLineSegment(sketch, "E59.top", {"start": v(-34.92, -20.64) * mm, "end": v(-38.1, -20.64) * mm});
            skLineSegment(sketch, "E59.right", {"start": v(-38.1, -7.94) * mm, "end": v(-38.1, -20.64) * mm});
            skLineSegment(sketch, "E60.bottom", {"start": v(-34.92, -26.99) * mm, "end": v(-38.1, -26.99) * mm});
            skLineSegment(sketch, "E60.top", {"start": v(-34.92, -39.69) * mm, "end": v(-38.1, -39.69) * mm});
            skLineSegment(sketch, "E60.right", {"start": v(-38.1, -26.99) * mm, "end": v(-38.1, -39.69) * mm});
            skLineSegment(sketch, "E61.trimOffspring", {"start": v(-34.92, -20.64) * mm, "end": v(-34.92, -26.99) * mm});
            skLineSegment(sketch, "E62.trimOffspring", {"start": v(-34.92, -39.69) * mm, "end": v(-34.92, -47.65) * mm});
            skLineSegment(sketch, "E63.trimOffspring", {"start": v(-12.7, -47.65) * mm, "end": v(12.7, -47.65) * mm});
            skLineSegment(sketch, "E64.trimOffspring", {"start": v(25.4, -47.65) * mm, "end": v(34.93, -47.65) * mm});
            skLineSegment(sketch, "E65.trimOffspring", {"start": v(25.4, 0) * mm, "end": v(34.93, 0) * mm});
            skLineSegment(sketch, "E66.trimOffspring", {"start": v(-12.7, 0) * mm, "end": v(12.7, 0) * mm});
            skSolve(sketch);
        }
        {
            var Q0;
            Q0=makeQuery(id+"F31.imprint","IMPRINT",FACE,{"disambiguationData":[TD([[makeQuery(id+"F31.imprint","IMPRINT",EDGE,{"derivedFrom":sQuery(id+"F31.wireOp",EDGE,"E54.top")}),1.0]])]});
            extrude(context, id + "F32", {"entities" : qUnion([Q0]), "oppositeDirection" : true, "depth" : (getVariable(context, 'ply')) * mm});
        }
        {
            var Q0;
            {var subQ0=sQuery(id+"F1.wireOp",EDGE,"E0.right");var subQ3=sQuery(id+"F1.wireOp",EDGE,"E0.bottom");Q0=makeQuery(id+"F9.boolean.opBoolean","SPLIT",FACE,{"disambiguationData":[TD([makeQuery(id+"F2.opExtrude","SWEPT_FACE",FACE,{"disambiguationData":[OSD([subQ0])]})])],"derivedFrom":makeQuery(id+"F2.opExtrude","SWEPT_FACE",FACE,{"disambiguationData":[OSD([subQ3])]})});}
            var sketch = newSketch(context, id + "F33", { "sketchPlane" : qUnion([Q0])});
            skLineSegment(sketch, "E67.bottom", {"start": v(-63.5, 0) * mm, "end": v(63.5, 0) * mm});
            skLineSegment(sketch, "E67.top", {"start": v(-63.5, -47.65) * mm, "end": v(63.5, -47.65) * mm});
            skLineSegment(sketch, "E67.left", {"start": v(-63.5, 0) * mm, "end": v(-63.5, -47.65) * mm});
            skLineSegment(sketch, "E67.right", {"start": v(63.5, 0) * mm, "end": v(63.5, -47.65) * mm});
            skLineSegment(sketch, "E68.bottom", {"start": v(-50.8, 0) * mm, "end": v(-38.1, 0) * mm});
            skLineSegment(sketch, "E68.top", {"start": v(-50.8, 3.18) * mm, "end": v(-38.1, 3.18) * mm});
            skLineSegment(sketch, "E68.left", {"start": v(-50.8, 0) * mm, "end": v(-50.8, 3.17) * mm});
            skLineSegment(sketch, "E68.right", {"start": v(-38.1, 0) * mm, "end": v(-38.1, 3.18) * mm});
            skLineSegment(sketch, "E69.bottom", {"start": v(-6.35, 0) * mm, "end": v(6.35, 0) * mm});
            skLineSegment(sketch, "E69.top", {"start": v(-6.35, 3.18) * mm, "end": v(6.35, 3.18) * mm});
            skLineSegment(sketch, "E69.left", {"start": v(-6.35, 0) * mm, "end": v(-6.35, 3.18) * mm});
            skLineSegment(sketch, "E69.right", {"start": v(6.35, 0) * mm, "end": v(6.35, 3.18) * mm});
            skLineSegment(sketch, "E70.bottom", {"start": v(38.1, 0) * mm, "end": v(50.8, 0) * mm});
            skLineSegment(sketch, "E70.top", {"start": v(38.1, 3.18) * mm, "end": v(50.8, 3.18) * mm});
            skLineSegment(sketch, "E70.left", {"start": v(38.1, 0) * mm, "end": v(38.1, 3.18) * mm});
            skLineSegment(sketch, "E70.right", {"start": v(50.8, 0) * mm, "end": v(50.8, 3.18) * mm});
            skLineSegment(sketch, "E71.bottom", {"start": v(-50.8, -47.65) * mm, "end": v(-38.1, -47.65) * mm});
            skLineSegment(sketch, "E71.top", {"start": v(-50.8, -50.83) * mm, "end": v(-38.1, -50.83) * mm});
            skLineSegment(sketch, "E71.left", {"start": v(-50.8, -47.65) * mm, "end": v(-50.8, -50.83) * mm});
            skLineSegment(sketch, "E71.right", {"start": v(-38.1, -47.65) * mm, "end": v(-38.1, -50.83) * mm});
            skLineSegment(sketch, "E72.bottom", {"start": v(-5.86, -47.65) * mm, "end": v(6.84, -47.65) * mm});
            skLineSegment(sketch, "E72.top", {"start": v(-6.27, -50.8) * mm, "end": v(6.43, -50.8) * mm});
            skLineSegment(sketch, "E72.left", {"start": v(-5.86, -47.65) * mm, "end": v(-6.27, -50.8) * mm});
            skLineSegment(sketch, "E72.right", {"start": v(6.84, -47.65) * mm, "end": v(6.43, -50.8) * mm});
            skLineSegment(sketch, "E73.bottom", {"start": v(38.03, -47.65) * mm, "end": v(50.73, -47.65) * mm});
            skLineSegment(sketch, "E73.top", {"start": v(38.03, -50.83) * mm, "end": v(50.73, -50.83) * mm});
            skLineSegment(sketch, "E73.left", {"start": v(38.03, -47.65) * mm, "end": v(38.03, -50.83) * mm});
            skLineSegment(sketch, "E73.right", {"start": v(50.73, -47.65) * mm, "end": v(50.73, -50.83) * mm});
            skSolve(sketch);
        }
        {
            var Q0;
            Q0 = qSketchRegion(id + "F33", true);
            extrude(context, id + "F34", {"entities" : qUnion([Q0]), "oppositeDirection" : true, "depth" : (getVariable(context, 'ply')) * mm});
        }
    });
